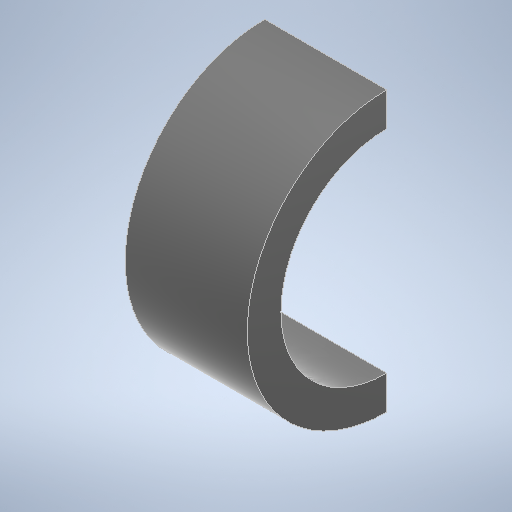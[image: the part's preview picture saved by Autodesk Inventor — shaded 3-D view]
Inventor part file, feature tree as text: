
AUTODESK INVENTOR PART (.ipt)
format: ipt  version: 2025.1 (Build 291241020, 241B)  size: 249,344 bytes
history: native  units: mm
features: sketch x2, revolve x1, extrude x1, projected_geometry x1
ambient origin geometry x8: Origin, YZ Plane, XZ Plane, XY Plane, X Axis, Y Axis, Z Axis, Center Point
bodies: Solid1 (feature_tree)
feature tree (5):
  revolve  "Revolution1"  [1 undecoded]
  extrude  "Extrusion1"  TaperAngle=90.0deg  [1 undecoded]
  sketch  "Sketch1"  dims[d0=6.07mm d1=8.0mm]
  sketch  "Sketch3"  dims[d2=7.0mm d3=90.0deg d4=10.0mm d5=10.0mm d6=0.0mm]
  projected_geometry  "Projected Loop1"
note: 2 required parameter values undecoded (feature->parameter linkage not recoverable at this tier; creation-order binding heuristic only, values carry confidence <= 0.55)